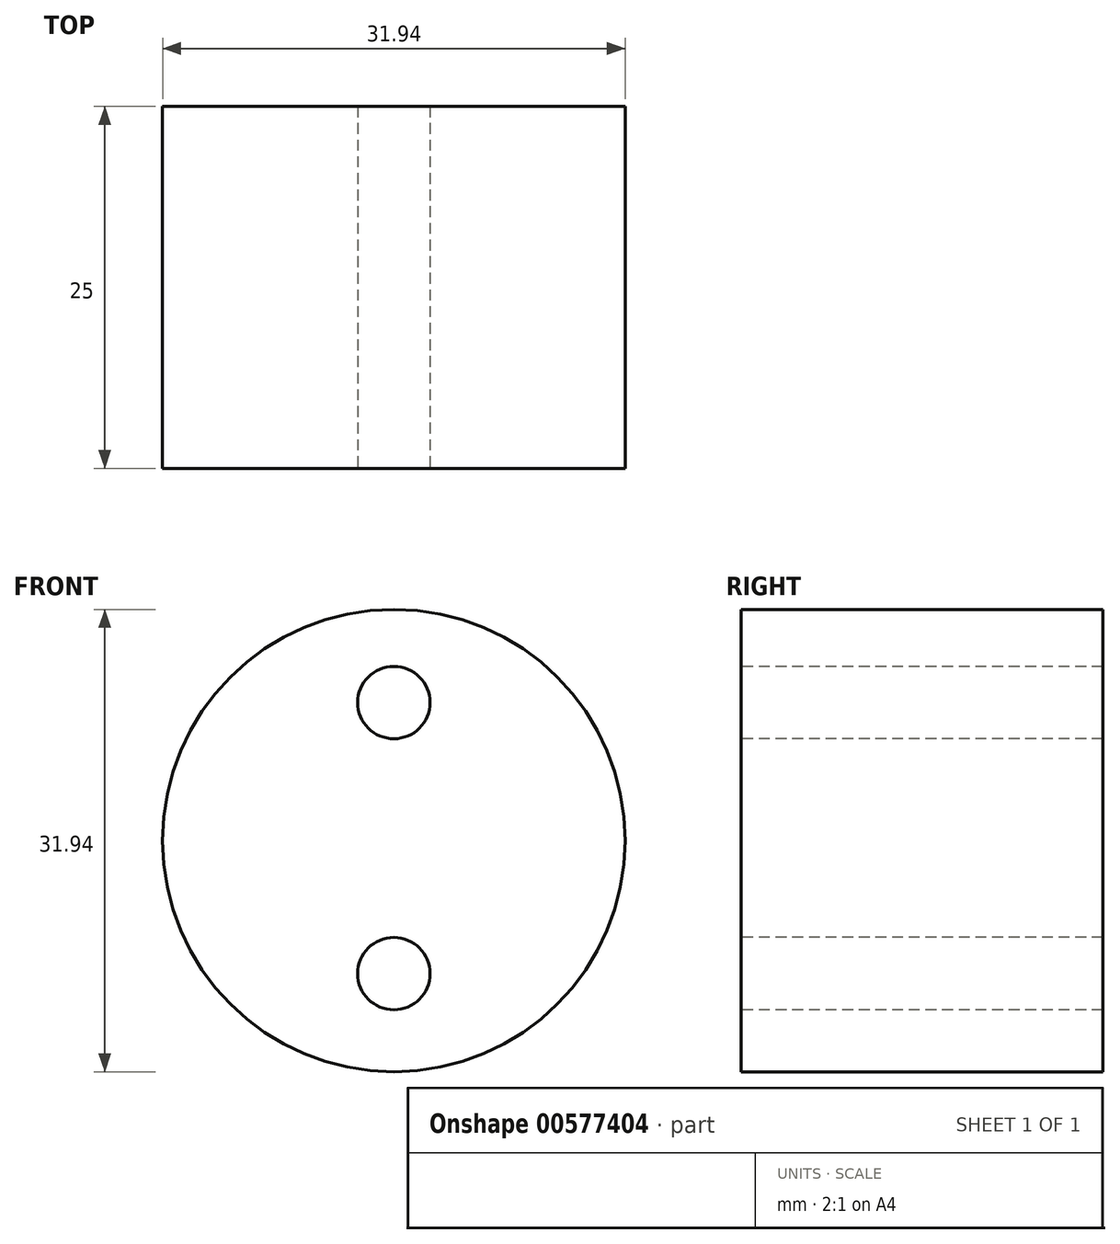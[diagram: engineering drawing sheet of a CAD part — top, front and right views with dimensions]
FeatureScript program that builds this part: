
annotation { "Feature Type Name" : "Feature", "Feature Type Description" : "" }
export const myFeature = defineFeature(function(context is Context, id is Id, definition is map)
    precondition{}
    {
        {
            var Q0;
            Q0=qCreatedBy(makeId("Front.planeOp"),FACE);
            var sketch = newSketch(context, id + "F0", { "sketchPlane" : qUnion([Q0])});
            skCircle(sketch, "E0", {"center": v(0, 0) * mm, "radius": 15.97 * mm});
            skSolve(sketch);
        }
        {
            var Q0;
            Q0=makeQuery(id+"F0.imprint","IMPRINT",FACE,{"disambiguationData":[TD([[makeQuery(id+"F0.imprint","IMPRINT",EDGE,{"derivedFrom":sQuery(id+"F0.wireOp",EDGE,"E0")}),1.0]])]});
            extrude(context, id + "F1", {"entities" : qUnion([Q0]), "depth" : 25 * mm, "offsetDistance" : 25 * mm});
        }
        {
            var Q0;
            Q0=makeQuery(id+"F1.opExtrude","CAP_FACE",FACE,{"disambiguationData":[OSD([sQuery(id+"F0.wireOp",EDGE,"E0")])],"isStart":false});
            var sketch = newSketch(context, id + "F2", { "sketchPlane" : qUnion([Q0])});
            skPoint(sketch, "E1", {"position": v(0, -9.2) * mm});
            skPoint(sketch, "E2", {"position": v(0, 9.53) * mm});
            skSolve(sketch);
        }
        {
            var Q0;
            Q0=sQuery(id+"F2.wireOp",VERTEX,"eb9ac328-77d3-4be2-981c-1beef63ed5db");
            var Q1;
            Q1=sQuery(id+"F2.wireOp",VERTEX,"49430798-3f6b-408d-9ab2-53a62a8efc6b");
            var Q2;
            Q2=sQuery(id+"F2.wireOp",VERTEX,"E2");
            var Q3;
            Q3=sQuery(id+"F2.wireOp",VERTEX,"E1");
            var Q4;
            Q4=makeQuery(id+"F1.opExtrude","SWEPT_BODY",BODY,{"disambiguationData":[OSD([sQuery(id+"F0.wireOp",EDGE,"E0")])]});
            hole(context, id + "F3", {"style" : HoleStyle.C_SINK, "endStyle" : HoleEndStyle.THROUGH, "holeDiameter" : 5 * mm, "cSinkDiameter" : 5 * mm, "cSinkAngle" : 90 * degree, "majorDiameter" : 5 * mm, "isTappedThrough" : true, "tappedDepth" : 12 * mm, "tapClearance" : 3, "startFromSketch" : true, "locations" : qUnion([Q0, Q1, Q2, Q3]), "scope" : qUnion([Q4])});
        }
    });
